# Revit family: Electronics_Expanders_Biamp_Tesira_TesiraCONNECT_Room-Connection-Device_TC___
name_source: partatom
category: Communication Devices
units: mm (PartAtom-declared; Revit-internal decimal feet)

## family parameters
Cut with Voids When Loaded = No
Host = Face
Maintain Annotation Orientation = No
OmniClass Number = 23.85.10.14
OmniClass Title = Visual Information Systems
Part Type = Normal
Room Calculation Point = No
Round Connector Dimension = Use Diameter
Shared = No

## types (2) — shared parameters
Altitude = 0-6,600 ft (0-2000m) MSL
Apparent Load = 132 VA
Compliance = FCC Part 15B (USA) UL and C-UL listed (USA and Canada) CE Marked (Europe) RoHS Directive (Europe) Evaluated to the requirements of UL 2043 and is suitable for use in air handling spaces
Connections - Connector Type = RJ-45
Connections - Number of PoE+ Powered Ports = 4
Connections - Number of Ports = 5
Connections - Supported Connection Speeds = 100Mbps, 1Gbps
Connections - Supported IEEE Protocols = 802.1, 802.1at, 802.1w, 802.1AS, 802.1BA, 802.1Qav, 802.3ab, 802.3af, 803.3u
Connector Description = 100-240VAC 50/60Hz
Cooling = Convection
Default Elevation = 4' - 0"
Depth = 0' - 5 25/32"
Height = 0' - 1 3/32"
Housing Material = Biamp - Plastic - Dark Gray
Humidity = 0-95% relative humidity (non-condensing)
Indicators - Front Panel = Power, Device Status, Fault, Port Status (per port)
Indicators - Rear Panel (per port) = Link, Activity
Manufacturer = Biamp
Max Power Consumption = 132 W
Maximum Daisychain Device Count = 4
Maximum Number of AVB Streams = 150
Maximum Number of Supported Endpoints = 13
No mount = No mount
Number of Poles = 1
Plenum Box 12x12 = Plenum Box 12x12
Power Factor = 1
Product Documentation Link = https://downloads.biamp.com
Product Page URL = https://www.biamp.com
Product data url = https://www.bimobject.com
RMX 100 Rack Shelf = RMX 100 Rack Shelf
Temperature Range = 32 - 104° F (0 – 40° C)
URL = https://www.biamp.com
Voltage = 120 V
Weight = 1.50 lbf
Width = 0' - 5 25/32"

## per-type parameters (varying)
| type | Description | Device | Maximum Number of Dante Channels | Model |
| TC-5 | TesiraCONNECT™ TC-5 Room Connection Device | TesiraCONNECT_TC : TC-5 |  | TesiraCONNECT - TC-5 |
| TC-5D | TesiraCONNECT™ TC-5D Room Connection Device with Dante™ | TesiraCONNECT_TC : TC-5D | 32x32 | TesiraCONNECT - TC-5D |

## geometry (parser evidence)
native form markers: Sweep x12
no freeform markers — native parametric forms only
